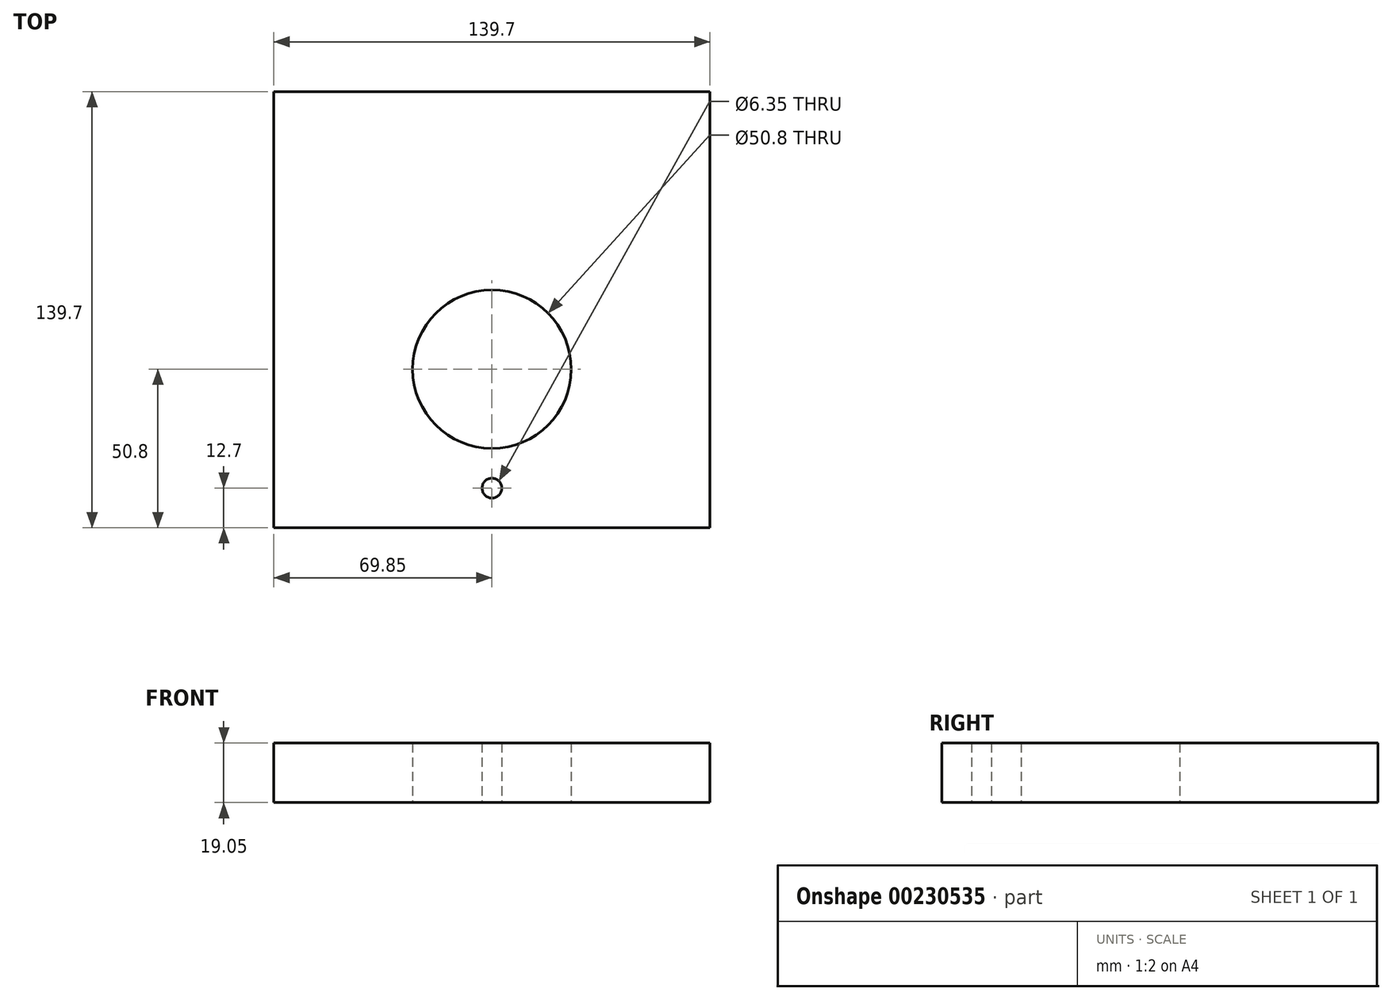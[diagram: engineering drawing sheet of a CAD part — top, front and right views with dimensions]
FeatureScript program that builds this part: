
annotation { "Feature Type Name" : "Feature", "Feature Type Description" : "" }
export const myFeature = defineFeature(function(context is Context, id is Id, definition is map)
    precondition{}
    {
        {
            var Q0;
            Q0=qCreatedBy(makeId("Top.planeOp"),FACE);
            var sketch = newSketch(context, id + "F0", { "sketchPlane" : qUnion([Q0])});
            skLineSegment(sketch, "E0.bottom", {"start": v(-69.85, -69.85) * mm, "end": v(69.85, -69.85) * mm});
            skLineSegment(sketch, "E0.top", {"start": v(-69.85, 69.85) * mm, "end": v(69.85, 69.85) * mm});
            skLineSegment(sketch, "E0.left", {"start": v(-69.85, -69.85) * mm, "end": v(-69.85, 69.85) * mm});
            skLineSegment(sketch, "E0.right", {"start": v(69.85, -69.85) * mm, "end": v(69.85, 69.85) * mm});
            skPoint(sketch, "E0.middle", {"position": v(0, 0) * mm});
            skLineSegment(sketch, "E1", {"start": v(0, -69.85) * mm, "end": v(0, -57.15) * mm});
            skPoint(sketch, "E1.endSnap0", {"position": v(0, -69.85) * mm});
            skLineSegment(sketch, "E2", {"start": v(0, -57.15) * mm, "end": v(0, -19.05) * mm});
            skCircle(sketch, "E3", {"center": v(0, -57.15) * mm, "radius": 3.18 * mm});
            skCircle(sketch, "E4", {"center": v(0, -19.05) * mm, "radius": 25.4 * mm});
            skSolve(sketch);
        }
        {
            var Q0;
            Q0 = qSketchRegion(id + "F0", true);
            extrude(context, id + "F1", {"entities" : qUnion([Q0]), "depth" : 19.05 * mm});
        }
    });
